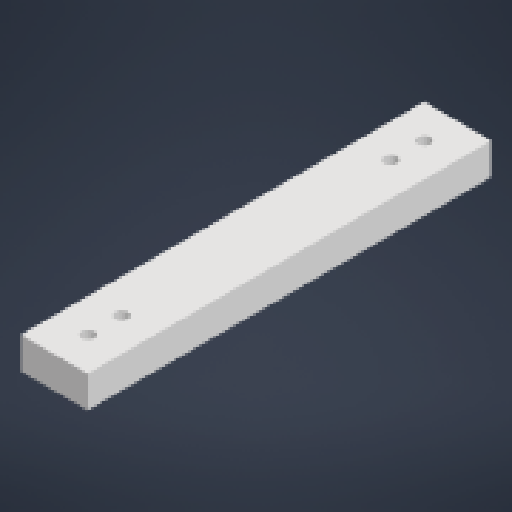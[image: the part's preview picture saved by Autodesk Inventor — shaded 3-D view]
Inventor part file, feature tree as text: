
AUTODESK INVENTOR PART (.ipt)
format: ipt  version: 2023 (Build 270158000, 158)  size: 126,976 bytes
history: native  units: in
note: dims shown in document units (in); Inventor stores cm internally (conversion verified against a paired STEP export)
features: extrude x1, sketch x1
ambient origin geometry x8: Origin, YZ Plane, XZ Plane, XY Plane, X Axis, Y Axis, Z Axis, Center Point
bodies: Solid1 (feature_tree)
feature tree (2):
  extrude  "Extrusion1"  Depth=6.0in
  sketch  "Sketch1"  dims[d0=1.0in d1=6.0in d2=1.0in d3=1.0in d4=90.0deg d5=0.1875in d6=0.1875in d7=0.1875in d8=0.1875in d9=0.47in d10=0.0in]
